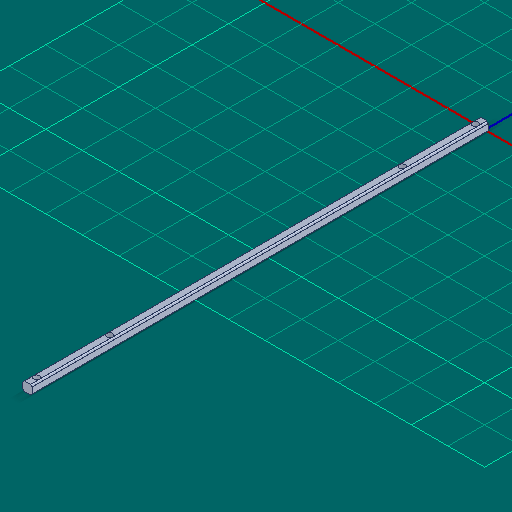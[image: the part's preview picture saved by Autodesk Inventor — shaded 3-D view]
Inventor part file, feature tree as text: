
AUTODESK INVENTOR PART (.ipt)
format: ipt  version: 2025 (Build 290162000, 162)  size: 210,432 bytes
history: native  units: in
note: dims shown in document units (in); Inventor stores cm internally (conversion verified against a paired STEP export)
features: other x50, extrude x3, sketch x3, thicken_offset x1
ambient origin geometry x8: Origin, YZ Plane, XZ Plane, XY Plane, X Axis, Y Axis, Z Axis, Center Point
bodies: Solid1 (feature_tree)
feature tree (57):
  other  "Table"
  other  "Shaft HS 0.5 in"
  other  "Shaft HS 1.0 in"
  other  "Shaft HS 1.5 in"
  other  "Shaft HS 2.0 in"
  other  "Shaft HS 2.5 in"
  other  "Shaft HS 3.0 in"
  other  "Shaft HS 3.5 in"
  other  "Shaft HS 4.0 in"
  other  "Shaft HS 4.5 in"
  other  "Shaft HS 5.0 in"
  other  "Shaft HS 5.5 in"
  other  "Shaft HS 6.0 in"
  other  "Shaft HS 6.5 in"
  other  "Shaft HS 7.0 in"
  other  "Shaft HS 7.5 in"
  other  "Shaft HS 8.0 in"
  other  "Shaft HS 8.5 in"
  other  "Shaft HS 9.0 in"
  other  "Shaft HS 9.5 in"
  other  "Shaft HS 10.0 in"
  other  "Shaft HS 10.5 in"
  other  "Shaft HS 11.0 in"
  other  "Shaft HS 11.5 in"
  other  "Shaft HS 12.0 in"
  other  "Shaft HS 12.5 in"
  other  "Shaft HS 13.0 in"
  other  "Shaft HS 13.5 in"
  other  "Shaft HS 14.0 in"
  other  "Shaft HS 14.5 in"
  other  "Shaft HS 15.0 in"
  other  "Shaft HS 15.5 in"
  other  "Shaft HS 16.0 in"
  other  "Shaft HS 16.5 in"
  other  "Shaft HS 17.0 in"
  other  "Shaft HS 17.5 in"
  other  "Shaft HS 18.0 in"
  other  "Shaft HS 18.5 in"
  other  "Shaft HS 19.0 in"
  other  "Shaft HS 19.5 in"
  other  "Shaft HS 20.0 in"
  other  "Shaft HS 20.5 in"
  other  "Shaft HS 21.0 in"
  other  "Shaft HS 21.5 in"
  other  "Shaft HS 22.0 in"
  other  "Shaft HS 22.5 in"
  other  "Shaft HS 23.0 in"
  other  "Shaft HS 23.5 in"
  other  "Shaft HS 24.0 in"
  extrude  "Extrusion1"  Depth=12.1875in
  thicken_offset  "Thicken1"
  extrude  "Extrusion2"  Depth=11.625in
  extrude  "Extrusion3"  Depth=0.165in
  sketch  "Sketch2"  dims[d0=0.0625in d1=0.0in d2=12.1875in]
  sketch  "Sketch3"  dims[d3=12.125in d4=11.625in]
  sketch  "Sketch4"  dims[d5=0.0in d6=0.165in d8=0.165in d9=1.0in d10=0.0in d11=0.165in d12=0.165in]
  other  "Cut-Revolve3"
